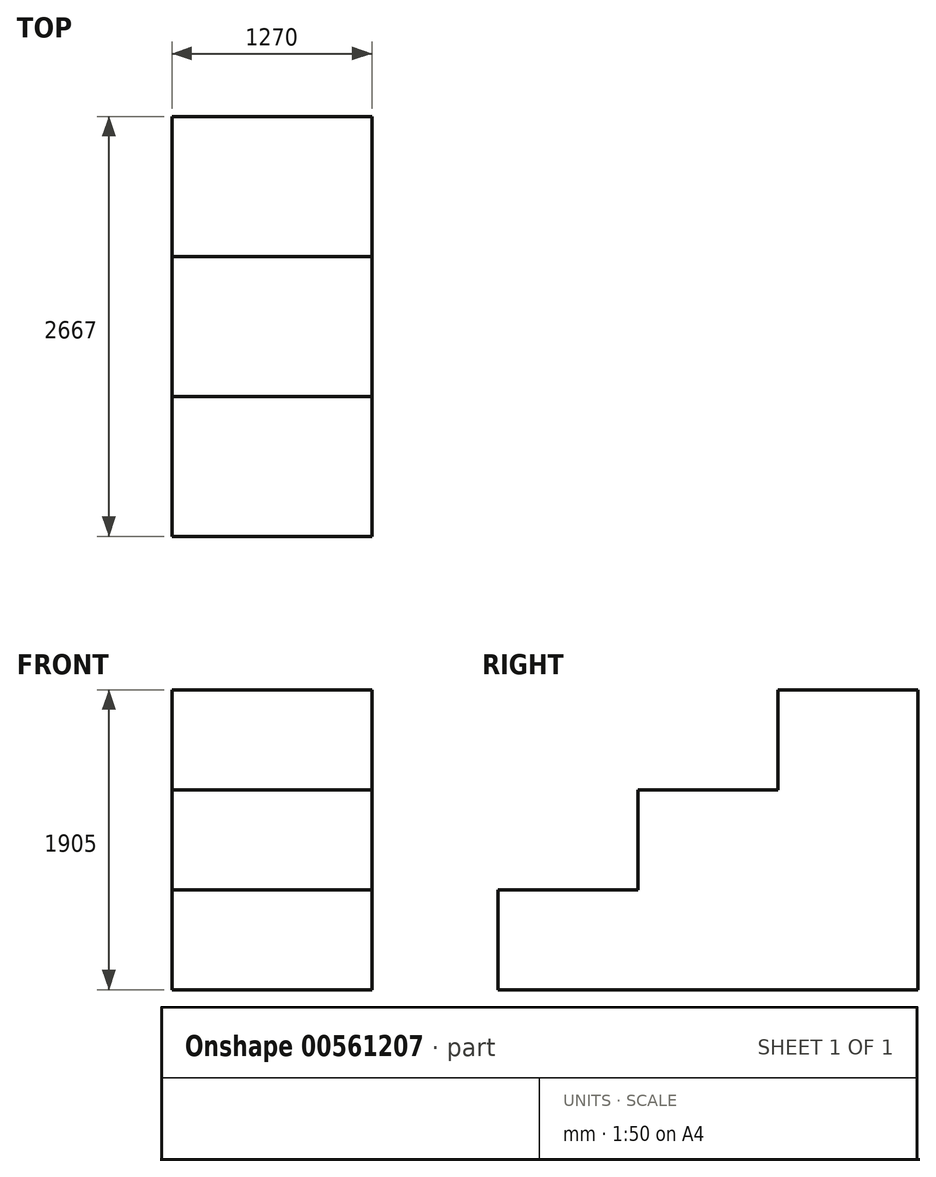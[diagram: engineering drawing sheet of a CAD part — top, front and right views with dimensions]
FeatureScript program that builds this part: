
annotation { "Feature Type Name" : "Feature", "Feature Type Description" : "" }
export const myFeature = defineFeature(function(context is Context, id is Id, definition is map)
    precondition{}
    {
        {
            var Q0;
            Q0=qCreatedBy(makeId("Right.planeOp"),FACE);
            var sketch = newSketch(context, id + "F0", { "sketchPlane" : qUnion([Q0])});
            skLineSegment(sketch, "E0.bottom", {"start": v(-87.58, -78.25) * mm, "end": v(2579.42, -78.25) * mm});
            skLineSegment(sketch, "E0.top", {"start": v(-87.58, 1826.75) * mm, "end": v(2579.42, 1826.75) * mm});
            skLineSegment(sketch, "E0.left", {"start": v(-87.58, -78.25) * mm, "end": v(-87.58, 1826.75) * mm});
            skLineSegment(sketch, "E0.right", {"start": v(2579.42, -78.25) * mm, "end": v(2579.42, 1826.75) * mm});
            skSolve(sketch);
        }
        {
            var Q0;
            Q0 = qSketchRegion(id + "F0", true);
            var Q1;
            Q1 = qSketchRegion(id + "FqS7TlovohoFv3x_1", true);
            extrude(context, id + "F1", {"entities" : qUnion([Q0, Q1]), "depth" : 1270 * mm, "offsetDistance" : 25.4 * mm});
        }
        {
            var Q0;
            Q0=makeQuery(id+"F1.opExtrude","CAP_FACE",FACE,{"disambiguationData":[OSD([sQuery(id+"F0.wireOp",EDGE,"E0.bottom"),sQuery(id+"F0.wireOp",EDGE,"E0.top"),sQuery(id+"F0.wireOp",EDGE,"E0.left"),sQuery(id+"F0.wireOp",EDGE,"E0.right")])],"isStart":false});
            var sketch = newSketch(context, id + "F2", { "sketchPlane" : qUnion([Q0])});
            skLineSegment(sketch, "E1", {"start": v(2579.42, 1826.75) * mm, "end": v(1690.42, 1826.75) * mm});
            skLineSegment(sketch, "E2", {"start": v(1690.42, 1826.75) * mm, "end": v(1690.42, 1191.75) * mm});
            skLineSegment(sketch, "E3", {"start": v(1690.42, 1191.75) * mm, "end": v(801.42, 1191.75) * mm});
            skLineSegment(sketch, "E4", {"start": v(801.42, 1191.75) * mm, "end": v(801.42, 556.75) * mm});
            skLineSegment(sketch, "E5", {"start": v(801.42, 556.75) * mm, "end": v(-87.58, 556.75) * mm});
            skSolve(sketch);
        }
        {
            var Q0;
            {var subQ1=sQuery(id+"F2.wireOp",EDGE,"E2");Q0=makeQuery(id+"F2.imprint","IMPRINT",FACE,{"disambiguationData":[TD([[makeQuery(id+"F2.imprint","IMPRINT",EDGE,{"derivedFrom":subQ1}),-1.0]])]});}
            extrude(context, id + "F3", {"entities" : qUnion([Q0]), "operationType" : NewBodyOperationType.REMOVE, "endBound" : BoundingType.THROUGH_ALL, "oppositeDirection" : true, "depth" : 1270 * mm, "offsetDistance" : 25.4 * mm});
        }
    });
